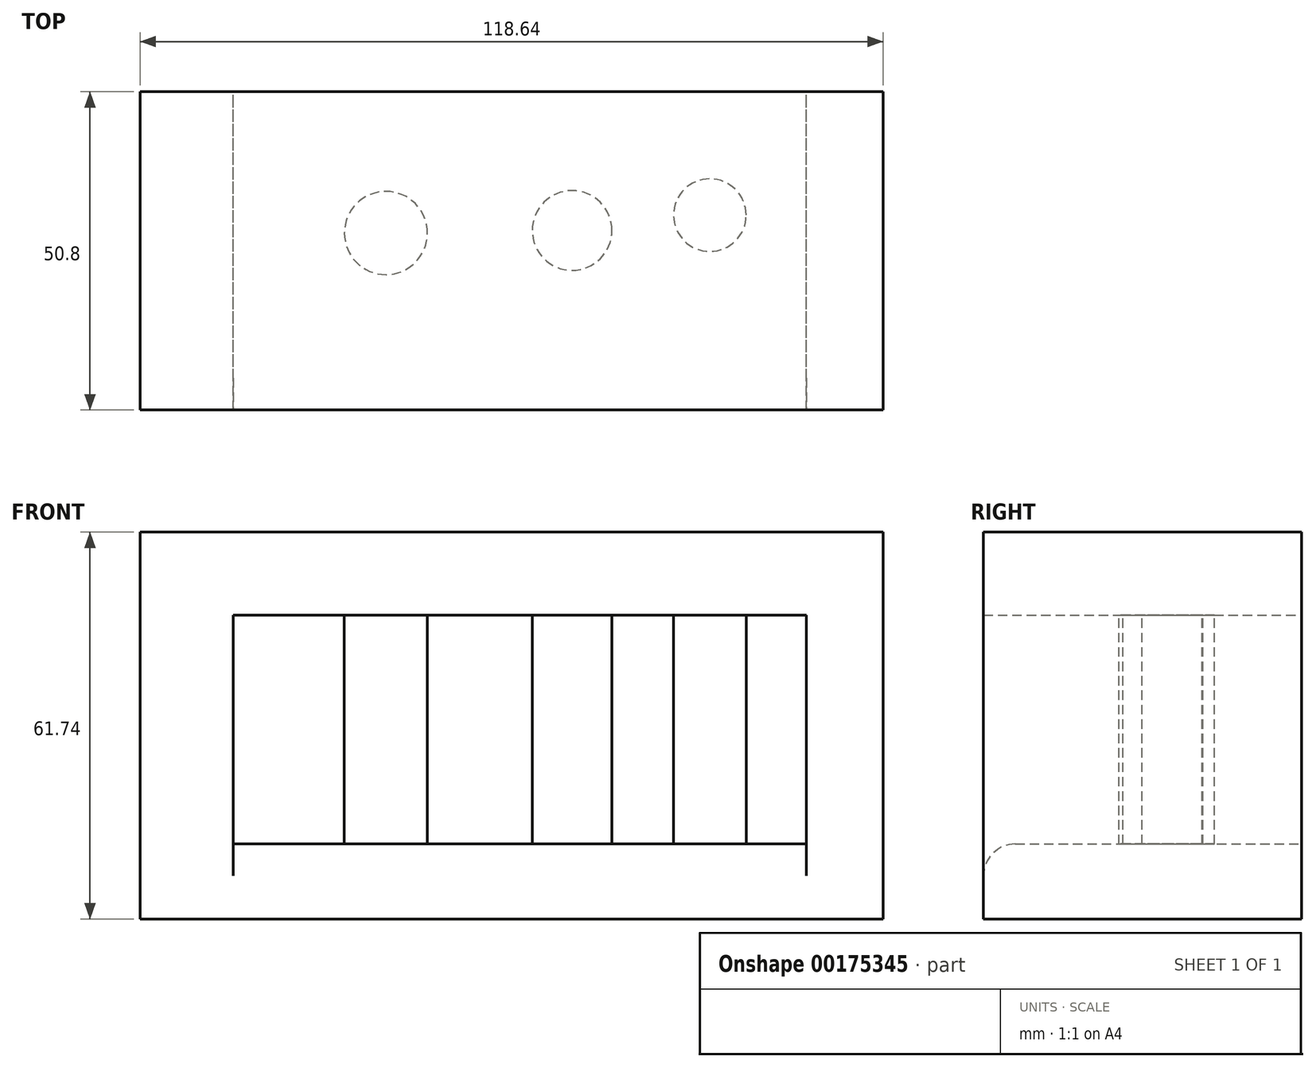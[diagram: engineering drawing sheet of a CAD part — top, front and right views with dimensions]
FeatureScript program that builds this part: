
annotation { "Feature Type Name" : "Feature", "Feature Type Description" : "" }
export const myFeature = defineFeature(function(context is Context, id is Id, definition is map)
    precondition{}
    {
        {
            var Q0;
            Q0=qCreatedBy(makeId("Front.planeOp"),FACE);
            var sketch = newSketch(context, id + "F0", { "sketchPlane" : qUnion([Q0])});
            skLineSegment(sketch, "E0.bottom", {"start": v(-30.06, 23.11) * mm, "end": v(88.58, 23.11) * mm});
            skLineSegment(sketch, "E0.top", {"start": v(-30.06, -38.63) * mm, "end": v(88.58, -38.63) * mm});
            skLineSegment(sketch, "E0.left", {"start": v(-30.06, 23.11) * mm, "end": v(-30.06, -38.63) * mm});
            skLineSegment(sketch, "E0.right", {"start": v(88.58, 23.11) * mm, "end": v(88.58, -38.63) * mm});
            skLineSegment(sketch, "E1.bottom", {"start": v(-15.2, 9.86) * mm, "end": v(76.3, 9.86) * mm});
            skLineSegment(sketch, "E1.top", {"start": v(-15.2, -26.67) * mm, "end": v(76.3, -26.67) * mm});
            skLineSegment(sketch, "E1.left", {"start": v(-15.2, 9.86) * mm, "end": v(-15.2, -26.67) * mm});
            skLineSegment(sketch, "E1.right", {"start": v(76.3, 9.86) * mm, "end": v(76.3, -26.67) * mm});
            skSolve(sketch);
        }
        {
            var Q0;
            Q0 = qSketchRegion(id + "F0", true);
            extrude(context, id + "F1", {"entities" : qUnion([Q0]), "depth" : 50.8 * mm});
        }
        {
            var Q0;
            Q0=makeQuery(id+"F1.opExtrude","SWEPT_FACE",FACE,{"disambiguationData":[OSD([sQuery(id+"F0.wireOp",EDGE,"E1.bottom")])]});
            var sketch = newSketch(context, id + "F2", { "sketchPlane" : qUnion([Q0])});
            skCircle(sketch, "E2", {"center": v(38.9, 22.14) * mm, "radius": 6.36 * mm});
            skCircle(sketch, "E3", {"center": v(60.9, 19.7) * mm, "radius": 5.79 * mm});
            skCircle(sketch, "E4", {"center": v(9.17, 22.55) * mm, "radius": 6.63 * mm});
            skSolve(sketch);
        }
        {
            var Q0;
            Q0 = qSketchRegion(id + "F2", true);
            extrude(context, id + "F3", {"entities" : qUnion([Q0]), "operationType" : NewBodyOperationType.ADD, "depth" : 48.26 * mm});
        }
        {
            var Q0;
            Q0=makeQuery(id+"F1.opExtrude","CAP_EDGE",EDGE,{"disambiguationData":[OSD([sQuery(id+"F0.wireOp",EDGE,"E1.top")])],"isStart":false});
            fillet(context, id + "F4", {"entities" : qUnion([Q0]), "radius" : 5.08 * mm, "tangentPropagation" : true, "allowEdgeOverflow" : false});
        }
    });
